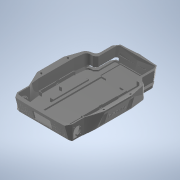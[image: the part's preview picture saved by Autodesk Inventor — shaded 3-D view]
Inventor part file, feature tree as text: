
AUTODESK INVENTOR PART (.ipt)
format: ipt  version: 2020 (Build 240168000, 168)  size: 7,460,352 bytes
history: native  units: mm
features: other x95, surface_op x82, extrude x24, sketch x21, mirror x8, projected_geometry x6, plane x5, fillet x4, chamfer x3, split x2, delete_face x1, shell x1, boolean_combine x1, move_body x1, hole x1, pattern_linear x1, loft x1
ambient origin geometry x8: Origin, YZ Plane, XZ Plane, XY Plane, X Axis, Y Axis, Z Axis, Center Point
bodies: Solid1 (feature_tree), Solid2 (feature_tree)
feature tree (257):
  other  "deck.ipt"
  delete_face  "Delete Face1"
  extrude  "Extrusion1"  Depth=1.5mm
  extrude  "Extrusion2"  Depth=3.0mm TaperAngle=0.0deg
  extrude  "Extrusion19"  Depth=1.5mm
  extrude  "Extrusion3"  Depth=62.0mm
  sketch  "Sketch3"  dims[d0=80.5mm d2=1.5mm]
  extrude  "Extrusion4"  Depth=39.6mm
  extrude  "Extrusion5"  Depth=2.0mm
  mirror  "Mirror1"
  plane  "Work Plane2"
  sketch  "Sketch4"  dims[d3=3.0mm d4=3.0mm d5=0.0mm]
  plane  "Work Plane3"
  extrude  "Extrusion6"  Depth=2.0mm
  extrude  "Extrusion7"  Depth=2.0mm
  fillet  "Fillet1"  Radius=2.0mm
  fillet  "Fillet2"  Radius=59.7mm
  plane  "Work Plane4"
  sketch  "Sketch7"  dims[d9=19.0mm d10=62.0mm]
  sketch  "Sketch8"  dims[d11=1.0mm d12=0.0mm d14=39.6mm]
  sketch  "Sketch9"  dims[d15=3.0mm d16=2.0mm]
  extrude  "Extrusion8"  Depth=3.0mm TaperAngle=0.0deg
  surface_op  "Sculpt1"
  shell  "Shell1"  Thickness=13.0mm
  boolean_combine  "Combine1"
  extrude  "Extrusion9"  Depth=32.2mm
  extrude  "Extrusion11"  Depth=5.0mm
  extrude  "Extrusion10"  Depth=19.0mm
  mirror  "Mirror2"
  chamfer  "Chamfer1"  Distance=6.0mm
  chamfer  "Chamfer2"  Distance=3.0mm
  move_body  "Move Body1"
  extrude  "Extrusion12"  Depth=6.0mm TaperAngle=0.0deg
  fillet  "Fillet3"  Radius=2.0mm
  extrude  "Extrusion13"  Depth=0.5mm
  extrude  "Extrusion14"  Depth=42.0mm
  mirror  "Mirror3"
  mirror  "Mirror4"
  hole  "Hole1"  [1 undecoded]
  plane  "Work Plane5"
  extrude  "Extrusion15"  Depth=15.0mm
  pattern_linear  "Rectangular Pattern1"  Spacing1=13.0mm  [1 undecoded]
  mirror  "Mirror5"
  extrude  "Extrusion16"  Depth=4.0mm
  extrude  "Extrusion17"  Depth=2.0mm TaperAngle=0.0deg
  split  "Split1"
  fillet  "Fillet5"  [1 undecoded]
  extrude  "Extrusion20"  TaperAngle=0.0deg  [1 undecoded]
  mirror  "Mirror7"
  extrude  "Extrusion21"  Depth=5.0mm
  extrude  "Extrusion22"  TaperAngle=0.0deg  [1 undecoded]
  chamfer  "Chamfer3"  Distance=5.0mm
  split  "Split2"
  extrude  "Extrusion23"  TaperAngle=0.0deg  [1 undecoded]
  mirror  "Mirror8"
  extrude  "Extrusion24"  Depth=3.0mm
  plane  "Work Plane6"
  sketch  "Sketch29"  dims[d47=1.0mm d49=6.0mm d50=0.0mm d51=3.0mm d52=6.0mm d53=0.0mm d54=2.0mm d55=0.5mm d56=42.0mm d57=2.0mm d58=15.0mm d59=13.0mm d60=4.0mm d61=2.0mm d62=0.0mm d63=0.0mm d64=90.0deg d65=0.0mm d66=90.0deg d100=5.0mm d101=0.0mm d102=5.0mm d103=0.0mm d104=3.0mm d105=10.0mm d106=0.0mm d107=10.0mm d108=0.0mm d109=10.0mm d110=0.0mm d111=2.5mm d112=2.0mm d113=45.0deg d114=2.5mm d115=2.0mm d116=45.0deg d117=10.0mm d118=385.0mm d119=0.0mm d120=0.0mm d121=54.0mm d122=0.0mm d123=7.5mm d124=15.0mm d125=80.0mm d127=5.5mm d128=6.0mm d129=4.0mm d130=2.0mm d131=90.0deg d132=8.0mm d133=20.594885mm d135=10.0mm d136=0.0mm d137=12.0mm d140=16.442mm d141=0.0mm d142=8.0mm d143=32.0mm d144=2.0mm d146=39.6mm d148=0.0mm d150=143.0mm d151=0.0mm d154=5.5mm d155=15.0mm d156=0.0mm d157=20.0mm d159=80.0mm d160=53.5mm d161=25.5mm d162=148.0mm d163=74.0mm d164=7.0mm d165=10.0mm d166=0.0mm d167=53.5mm d168=26.75mm d170=10.0mm d171=25.5mm d172=12.75mm d173=10.0mm d174=0.0mm d175=59.0mm d176=2.5mm d177=2.0mm d180=2.0mm d181=68.0mm d183=1.5mm d184=3.0mm d187=7.0mm d188=0.0mm d190=32.0mm d191=17.0mm d192=5.0mm d193=7.0mm d194=10.0mm d195=0.0mm d196=95.0mm d197=7.0mm d198=1.5mm d199=0.0mm d200=183.5mm d201=7.0mm d203=4.2mm d204=10.0mm d205=44.0mm d206=1.5mm d207=10.0mm d208=8.0mm d209=0.0mm d210=8.0mm d211=2.0mm d212=45.0deg d213=1.0mm d214=0.0mm d215=1.0mm d216=1.5mm d217=2.0mm d218=2.5mm d220=3.0mm d222=1.5mm d223=1.5mm d224=1.5mm d226=1.0mm d227=0.0mm d228=1.5mm d230=2.0mm d231=1.5mm d232=1.5mm d233=1.5mm d234=0.5mm d235=0.6mm d236=1.5mm d237=0.8mm d238=1.5mm d239=0.9mm d242=1.5mm d243=1.5mm d244=0.8mm d245=1.5mm d246=0.6mm d247=1.5mm d248=3.5mm d249=4.0mm d250=1.5mm d251=1.5mm d252=1.5mm d253=1.5mm d254=3.5mm d255=4.0mm d256=1.5mm d257=1.5mm d258=1.5mm d259=1.5mm d260=210.0mm d262=6.775mm d263=10.0mm d265=10.0mm d267=1.5mm d268=1.5mm d269=3.0435mm d270=3.043244mm d271=0.5mm d272=0.0mm d273=1.0mm d274=1.5mm d275=2.0mm d276=2.5mm d277=3.0mm d278=1.5mm d279=1.5mm d280=1.5mm d281=1.0mm d282=0.0mm d283=1.5mm d284=2.0mm d285=1.5mm d286=1.5mm d287=1.5mm d288=0.5mm d289=0.6mm d290=1.5mm d291=0.8mm d292=1.5mm d293=0.9mm d294=1.5mm d295=1.5mm d296=0.8mm d297=1.5mm d298=0.6mm d299=1.5mm d300=3.5mm d301=4.0mm d302=1.5mm d303=1.5mm d304=3.5mm d305=4.0mm d306=1.5mm d307=1.5mm d308=1.5mm d309=1.5mm d310=1.5mm d311=1.5mm d312=1.5mm d313=170.0mm d315=6.7mm d316=10.0mm d318=10.0mm d320=1.5mm d321=1.62mm d322=1.619738mm d323=0.5mm d324=0.5mm d325=0.0mm d326=0.0mm d327=0.0mm d328=0.0mm d329=0.0mm d330=0.0mm d331=0.0mm d332=0.0mm d333=0.0mm d334=0.0mm d335=0.0mm d336=0.0mm d337=0.0mm d338=0.0mm d339=0.0mm d340=0.0mm d341=0.0mm d342=0.0mm d343=0.0mm d344=0.0mm d345=0.0mm d346=0.0mm d347=0.0mm d348=0.0mm d349=0.0mm d350=0.0mm d351=0.0mm d352=0.0mm d353=0.0mm d354=0.0mm d355=0.0mm d356=0.0mm d357=0.0mm d358=0.0mm d359=0.0mm d360=0.0mm d361=0.0mm d362=0.0mm d363=0.0mm d364=0.0mm d365=0.0mm d366=0.0mm d367=0.0mm d368=0.0mm d369=0.0mm d370=0.0mm d371=0.0mm d372=0.0mm d373=0.0mm d374=0.0mm d375=0.0mm d376=0.0mm d377=0.0mm d378=0.0mm d379=0.0mm d380=0.0mm d381=0.0mm d382=0.0mm d383=0.0mm d384=0.0mm d385=0.0mm d386=0.0mm d387=0.0mm d388=0.0mm d389=0.0mm d390=0.0mm d391=0.0mm d392=0.0mm d393=0.0mm d394=0.0mm d395=0.0mm d396=0.0mm d397=0.0mm d398=0.0mm d399=0.0mm d400=0.0mm d401=0.0mm d134=1.0mm d138=5.5mm d139=0.375mm d145=0.375mm]
  sketch  "3D Sketch2"
  sketch  "3D Sketch3"
  surface_op  "Sculpt2"
  mirror  "Mirror9"
  sketch  "Sketch6"  dims[d6=9.0mm d7=0.0mm d8=1.5mm]
  other  "Edges1"
  other  "Srf1"
  other  "Srf16"
  other  "Srf17"
  sketch  "Sketch10"  dims[d17=103.0mm d18=2.0mm]
  projected_geometry  "Projected Loop1"
  sketch  "Sketch11"  dims[d19=7.0mm d21=2.0mm d22=2.0mm d23=59.7mm]
  projected_geometry  "Projected Loop2"
  sketch  "Sketch12"  dims[d24=7.0mm d26=3.0mm d27=0.0mm d28=13.0mm d29=0.0mm]
  other  "Front Profile"
  other  "Srf18"
  sketch  "Sketch18"  dims[d30=25.7mm d31=32.2mm]
  projected_geometry  "Projected Loop3"
  sketch  "Sketch20"  dims[d32=23.0mm d33=5.0mm]
  other  "Work Axis1"
  other  "Work Axis2"
  sketch  "Sketch21"  dims[d34=-3.5mm d35=19.0mm]
  sketch  "Sketch22"  dims[d36=25.0mm]
  sketch  "Sketch24"  dims[d38=3.5mm]
  projected_geometry  "Projected Loop5"
  sketch  "Sketch25"  dims[d39=2.0mm]
  projected_geometry  "Projected Loop6"
  projected_geometry  "Projected Loop7"
  sketch  "Sketch26"  dims[d43=-3.5mm]
  sketch  "Sketch27"  dims[d44=12.6mm]
  sketch  "Sketch28"  dims[d45=7.0mm]
  other  "Project to Surface1"
  other  "Srf20"
  other  "Project to Surface2"
  other  "Srf21"
  other  "Srf22"
  other  "Srf23"
  other  "Srf24"
  other  "Srf25"
  other  "Srf26"
  other  "Srf27"
  other  "Srf28"
  other  "Srf29"
  other  "Srf30"
  other  "Srf31"
  other  "Srf32"
  other  "Srf33"
  other  "Srf34"
  other  "Srf35"
  other  "Srf36"
  other  "Srf37"
  other  "Srf38"
  other  "Srf39"
  other  "Srf40"
  other  "Srf41"
  other  "Srf42"
  other  "Srf43"
  other  "Srf44"
  other  "Srf45"
  other  "Srf46"
  other  "Srf47"
  other  "Srf48"
  other  "Srf49"
  other  "Srf50"
  other  "Srf51"
  other  "Srf52"
  other  "Srf53"
  other  "Srf54"
  other  "Srf55"
  other  "Srf56"
  other  "Srf57"
  other  "Srf58"
  other  "Srf59"
  other  "Srf60"
  other  "Srf61"
  other  "Srf62"
  other  "Srf63"
  other  "Srf64"
  other  "Srf65"
  other  "Srf66"
  other  "Srf67"
  other  "Srf68"
  other  "Srf69"
  other  "Srf70"
  other  "Srf71"
  other  "Srf72"
  other  "Srf73"
  other  "Srf74"
  other  "Srf75"
  other  "Srf76"
  other  "Srf77"
  other  "Srf78"
  other  "Srf79"
  other  "Srf80"
  other  "Srf81"
  other  "Srf82"
  other  "Srf83"
  other  "Srf84"
  other  "Srf85"
  other  "Srf86"
  other  "Srf87"
  other  "Srf88"
  other  "Srf89"
  other  "Srf90"
  other  "Srf91"
  other  "Srf92"
  other  "Srf93"
  other  "Srf94"
  other  "Srf95"
  other  "Srf96"
  other  "Srf97"
  extrude  "ExtrusionSrf1"  Depth=10.0mm TaperAngle=0.0deg
  surface_op  "Surface1"
  other  "OffsetSrf2"
  loft  "LoftSrf1"
  surface_op  "Boundary Patch13"
  surface_op  "Boundary Patch14"
  other  "Srf19"
  surface_op  "Boundary Patch15"
  surface_op  "Boundary Patch16"
  surface_op  "Boundary Patch17"
  surface_op  "Boundary Patch18"
  surface_op  "Boundary Patch19"
  surface_op  "Boundary Patch20"
  surface_op  "Boundary Patch22"
  surface_op  "Boundary Patch23"
  surface_op  "Boundary Patch24"
  surface_op  "Boundary Patch25"
  surface_op  "Boundary Patch26"
  surface_op  "Boundary Patch27"
  surface_op  "Boundary Patch28"
  surface_op  "Boundary Patch29"
  surface_op  "Boundary Patch30"
  surface_op  "Boundary Patch31"
  surface_op  "Boundary Patch32"
  surface_op  "Boundary Patch33"
  surface_op  "Boundary Patch34"
  surface_op  "Boundary Patch35"
  surface_op  "Boundary Patch36"
  surface_op  "Boundary Patch37"
  surface_op  "Boundary Patch38"
  surface_op  "Boundary Patch39"
  surface_op  "Boundary Patch40"
  surface_op  "Boundary Patch41"
  surface_op  "Boundary Patch42"
  surface_op  "Boundary Patch43"
  surface_op  "Boundary Patch44"
  surface_op  "Boundary Patch45"
  surface_op  "Boundary Patch46"
  surface_op  "Boundary Patch47"
  surface_op  "Boundary Patch48"
  surface_op  "Boundary Patch49"
  surface_op  "Boundary Patch50"
  surface_op  "Boundary Patch51"
  surface_op  "Boundary Patch52"
  surface_op  "Boundary Patch53"
  surface_op  "Boundary Patch54"
  surface_op  "Boundary Patch55"
  surface_op  "Boundary Patch56"
  surface_op  "Boundary Patch57"
  surface_op  "Boundary Patch58"
  surface_op  "Boundary Patch59"
  surface_op  "Boundary Patch60"
  surface_op  "Boundary Patch61"
  surface_op  "Boundary Patch62"
  surface_op  "Boundary Patch63"
  surface_op  "Boundary Patch64"
  surface_op  "Boundary Patch65"
  surface_op  "Boundary Patch66"
  surface_op  "Boundary Patch67"
  surface_op  "Boundary Patch68"
  surface_op  "Boundary Patch69"
  surface_op  "Boundary Patch70"
  surface_op  "Boundary Patch71"
  surface_op  "Boundary Patch72"
  surface_op  "Boundary Patch73"
  surface_op  "Boundary Patch74"
  surface_op  "Boundary Patch75"
  surface_op  "Boundary Patch76"
  surface_op  "Boundary Patch77"
  surface_op  "Boundary Patch78"
  surface_op  "Boundary Patch79"
  surface_op  "Boundary Patch80"
  surface_op  "Boundary Patch81"
  surface_op  "Boundary Patch82"
  surface_op  "Boundary Patch83"
  surface_op  "Boundary Patch84"
  surface_op  "Boundary Patch85"
  surface_op  "Boundary Patch86"
  surface_op  "Boundary Patch87"
  surface_op  "Boundary Patch88"
  surface_op  "Boundary Patch89"
  surface_op  "Boundary Patch90"
  surface_op  "Boundary Patch91"
  surface_op  "Boundary Patch21"
  parser-record x1  (decoder bookkeeping rows leaked as tree rows — omitted from the tree; the rows remain in map.json)
  other  "Housing v3.iam"
  other  "Receiver:1"
  other  "Receiver Case:1"
note: 6 required parameter values undecoded (feature->parameter linkage not recoverable at this tier; creation-order binding heuristic only, values carry confidence <= 0.55)
note: 1 file-system path scrubbed to <path> (originals preserved in map.json)
